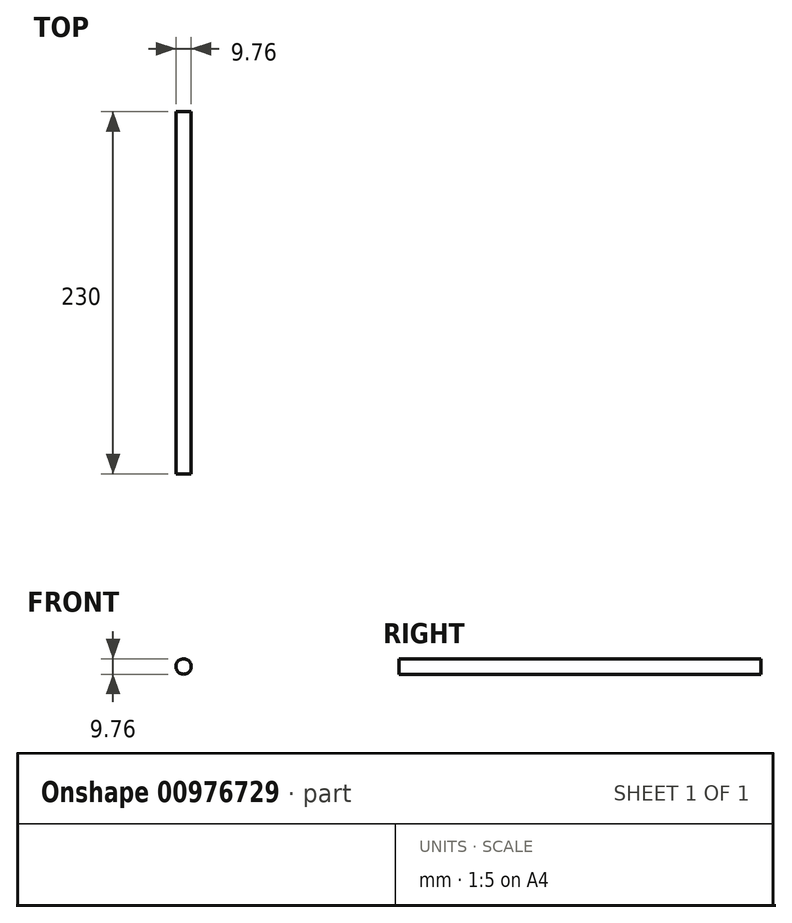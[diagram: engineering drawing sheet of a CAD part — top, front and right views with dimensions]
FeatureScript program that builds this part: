
annotation { "Feature Type Name" : "Feature", "Feature Type Description" : "" }
export const myFeature = defineFeature(function(context is Context, id is Id, definition is map)
    precondition{}
    {
        {
            var Q0;
            Q0=qCreatedBy(makeId("Front.planeOp"),FACE);
            var sketch = newSketch(context, id + "F0", { "sketchPlane" : qUnion([Q0])});
            skCircle(sketch, "E0", {"center": v(0, 0) * mm, "radius": 4.88 * mm});
            skSolve(sketch);
        }
        {
            var Q0;
            Q0=makeQuery(id+"F0.imprint","IMPRINT",FACE,{"disambiguationData":[TD([[makeQuery(id+"F0.imprint","IMPRINT",EDGE,{"derivedFrom":sQuery(id+"F0.wireOp",EDGE,"E0")}),1.0]])]});
            extrude(context, id + "F1", {"entities" : qUnion([Q0]), "depth" : 230 * mm, "offsetDistance" : 25 * mm});
        }
    });
